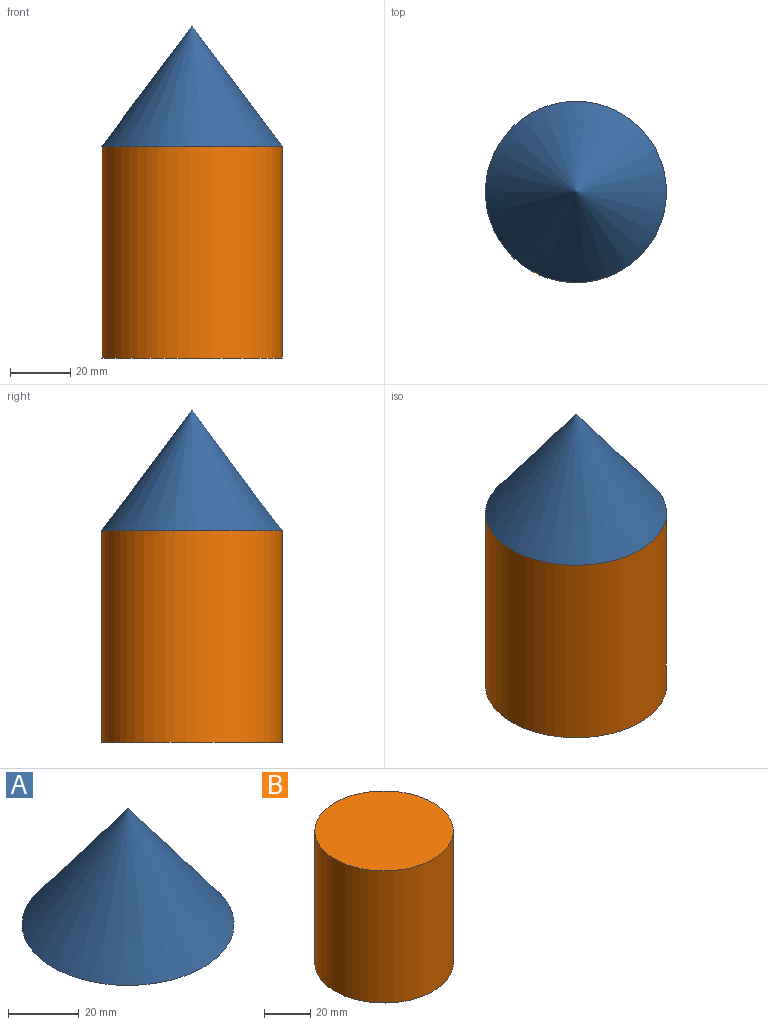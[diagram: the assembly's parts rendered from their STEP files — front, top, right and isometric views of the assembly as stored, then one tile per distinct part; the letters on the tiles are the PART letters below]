
ASSEMBLY  parts=2 mates=1
PART A: 3 faces, bbox 60x60x40 mm
  f0: cone r=30mm half-angle=36.8deg, axis (0,0,-1), area 4720mm2, adj f1,f2
  f1: plane 0.15x0.15mm, normal (0,0,1), area 0mm2, adj f0
  f2: plane 60x60mm, normal (0,0,-1), area 2827.4mm2, adj f0
PART B: 3 faces, bbox 60x60x70 mm
  f0: cylinder r=30mm len=70mm, axis (0,0,-1), area 13194.7mm2, adj f1,f2
  f1: plane 60x60mm, normal (0,0,1), area 2827.4mm2, adj f0
  f2: plane 60x60mm, normal (0,0,-1), area 2827.4mm2, adj f0
PLACE A t=(-117.66,-1.75,69.75)mm
PLACE B t=(-0.57,-1.75,-0.25)mm
MATE fastened A.f0 <-> B.f0  axis (0,0,-1) through (-0.57,-1.75,69.75)mm
